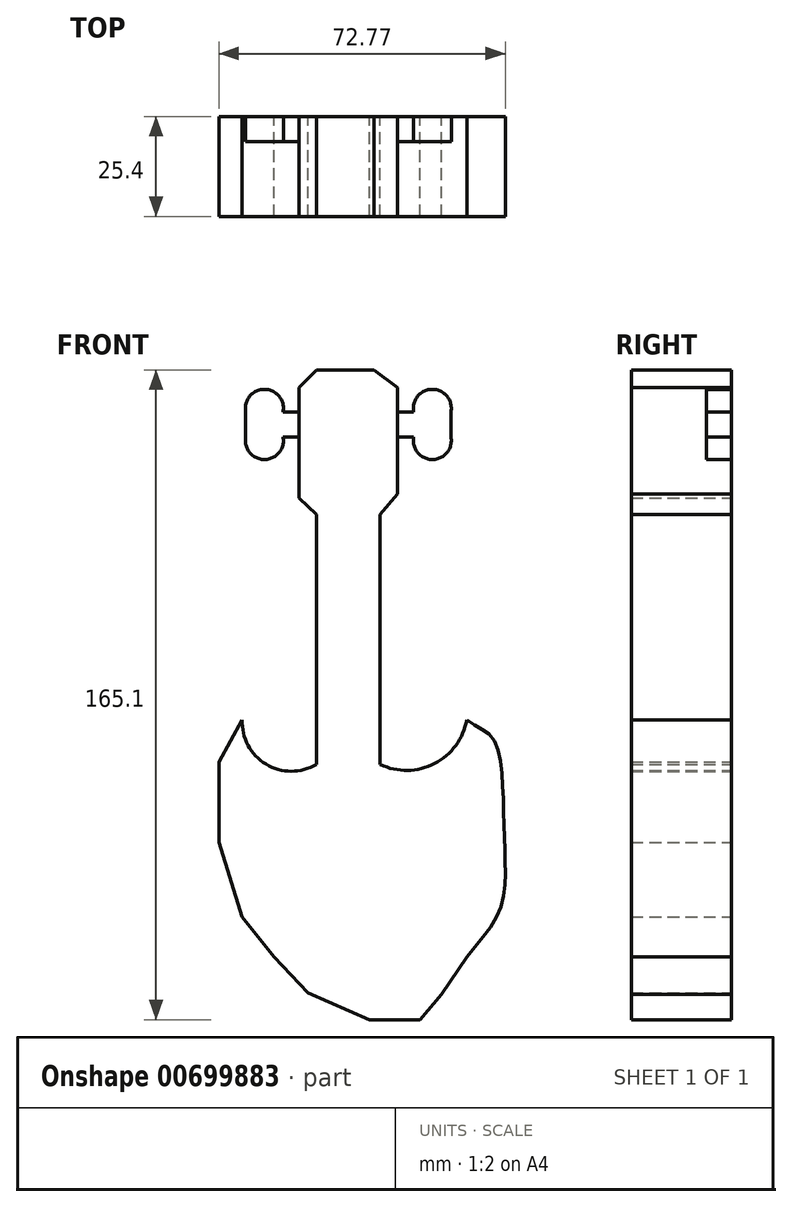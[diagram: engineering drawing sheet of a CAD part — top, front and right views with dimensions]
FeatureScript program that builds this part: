
annotation { "Feature Type Name" : "Feature", "Feature Type Description" : "" }
export const myFeature = defineFeature(function(context is Context, id is Id, definition is map)
    precondition{}
    {
        {
            var Q0;
            Q0=qCreatedBy(makeId("Front.planeOp"),FACE);
            var sketch = newSketch(context, id + "F0", { "sketchPlane" : qUnion([Q0])});
            skLineSegment(sketch, "E0", {"start": v(-16.22, 78) * mm, "end": v(-16.22, 14.5) * mm});
            skLineSegment(sketch, "E1", {"start": v(0, 78) * mm, "end": v(0, 14.5) * mm});
            skArc(sketch, "E2", {"start": v(-35.06, 25.87) * mm, "mid": v(-29.02, 14.58) * mm, "end": v(-16.22, 14.5) * mm});
            skLineSegment(sketch, "E3", {"start": v(-35.06, 25.87) * mm, "end": v(-40.98, 15.11) * mm});
            skLineSegment(sketch, "E4", {"start": v(-40.98, 15.11) * mm, "end": v(-40.98, -5.34) * mm});
            skLineSegment(sketch, "E5", {"start": v(-40.98, -5.34) * mm, "end": v(-35.06, -24.17) * mm});
            skLineSegment(sketch, "E6", {"start": v(-35.06, -24.17) * mm, "end": v(-26.98, -34.4) * mm});
            skLineSegment(sketch, "E7", {"start": v(-26.98, -34.4) * mm, "end": v(-18.37, -43.54) * mm});
            skLineSegment(sketch, "E8", {"start": v(-18.37, -43.54) * mm, "end": v(-2.77, -50.33) * mm});
            skLineSegment(sketch, "E9", {"start": v(-2.77, -50.33) * mm, "end": v(10.15, -50.33) * mm});
            skLineSegment(sketch, "E10", {"start": v(10.15, -50.33) * mm, "end": v(15.53, -43.87) * mm});
            skLineSegment(sketch, "E11", {"start": v(15.53, -43.87) * mm, "end": v(21.99, -34.4) * mm});
            skFitSpline(sketch, "E12", {"points": [v(21.99, -34.4) * mm, v(30.6, -21.72) * mm, v(31.67, -8.27) * mm, v(31.14, 8.41) * mm, v(28.44, 21.33) * mm, v(21.99, 25.87) * mm], "startDerivative": vector(49.4, 59.04) * mm, "endDerivative": vector(-43.97, 36.62) * mm});
            skArc(sketch, "E13", {"start": v(0, 14.5) * mm, "mid": v(13.8, 14.75) * mm, "end": v(21.99, 25.87) * mm});
            skLineSegment(sketch, "E14", {"start": v(-16.22, 78) * mm, "end": v(-20.62, 82.2) * mm});
            skLineSegment(sketch, "E15", {"start": v(-20.62, 82.2) * mm, "end": v(-20.62, 97.73) * mm});
            skLineSegment(sketch, "E16", {"start": v(-20.62, 104.08) * mm, "end": v(-20.62, 110.26) * mm});
            skLineSegment(sketch, "E17", {"start": v(-20.62, 110.26) * mm, "end": v(-16.22, 114.77) * mm});
            skLineSegment(sketch, "E18", {"start": v(-16.22, 114.77) * mm, "end": v(-1.58, 114.77) * mm});
            skLineSegment(sketch, "E19", {"start": v(-1.58, 114.77) * mm, "end": v(4.44, 110.26) * mm});
            skLineSegment(sketch, "E20", {"start": v(4.44, 110.26) * mm, "end": v(4.44, 104.08) * mm});
            skLineSegment(sketch, "E21", {"start": v(4.44, 97.73) * mm, "end": v(4.44, 83.2) * mm});
            skLineSegment(sketch, "E22", {"start": v(4.44, 83.2) * mm, "end": v(0, 78) * mm});
            skLineSegment(sketch, "E23", {"start": v(-20.62, 104.08) * mm, "end": v(-24.68, 104.08) * mm});
            skArc(sketch, "E24", {"start": v(-24.68, 104.08) * mm, "mid": v(-29.42, 109.83) * mm, "end": v(-34.16, 104.08) * mm});
            skLineSegment(sketch, "E25", {"start": v(-20.62, 97.73) * mm, "end": v(-24.68, 97.73) * mm});
            skLineSegment(sketch, "E26", {"start": v(-34.16, 104.08) * mm, "end": v(-34.16, 97.73) * mm});
            skArc(sketch, "E27", {"start": v(-34.16, 97.73) * mm, "mid": v(-29.42, 91.98) * mm, "end": v(-24.68, 97.73) * mm});
            skLineSegment(sketch, "E28", {"start": v(4.44, 104.08) * mm, "end": v(8.5, 104.08) * mm});
            skLineSegment(sketch, "E29", {"start": v(4.44, 97.73) * mm, "end": v(8.5, 97.73) * mm});
            skArc(sketch, "E30", {"start": v(17.97, 104.08) * mm, "mid": v(13.24, 109.83) * mm, "end": v(8.5, 104.08) * mm});
            skLineSegment(sketch, "E31", {"start": v(17.97, 104.08) * mm, "end": v(17.97, 97.73) * mm});
            skArc(sketch, "E32", {"start": v(8.5, 97.73) * mm, "mid": v(13.24, 91.98) * mm, "end": v(17.97, 97.73) * mm});
            skLineSegment(sketch, "E33", {"start": v(-20.62, 104.08) * mm, "end": v(-20.62, 97.73) * mm});
            skLineSegment(sketch, "E34", {"start": v(4.44, 104.08) * mm, "end": v(4.44, 97.73) * mm});
            skSolve(sketch);
        }
        {
            var Q0;
            Q0=makeQuery(id+"F0.imprint","IMPRINT",FACE,{"disambiguationData":[TD([[makeQuery(id+"F0.imprint","IMPRINT",EDGE,{"derivedFrom":sQuery(id+"F0.wireOp",EDGE,"E0")}),1.0]])]});
            extrude(context, id + "F1", {"entities" : qUnion([Q0]), "depth" : 25.4 * mm, "offsetDistance" : 25.4 * mm});
        }
        {
            var Q0;
            Q0=makeQuery(id+"F0.imprint","IMPRINT",FACE,{"disambiguationData":[TD([[makeQuery(id+"F0.imprint","IMPRINT",EDGE,{"derivedFrom":sQuery(id+"F0.wireOp",EDGE,"E23")}),1.0]])]});
            var Q1;
            Q1=makeQuery(id+"F0.imprint","IMPRINT",FACE,{"disambiguationData":[TD([[makeQuery(id+"F0.imprint","IMPRINT",EDGE,{"derivedFrom":sQuery(id+"F0.wireOp",EDGE,"E28")}),-1.0]])]});
            extrude(context, id + "F2", {"entities" : qUnion([Q0, Q1]), "operationType" : NewBodyOperationType.ADD, "depth" : 6.35 * mm, "offsetDistance" : 25.4 * mm});
        }
    });
